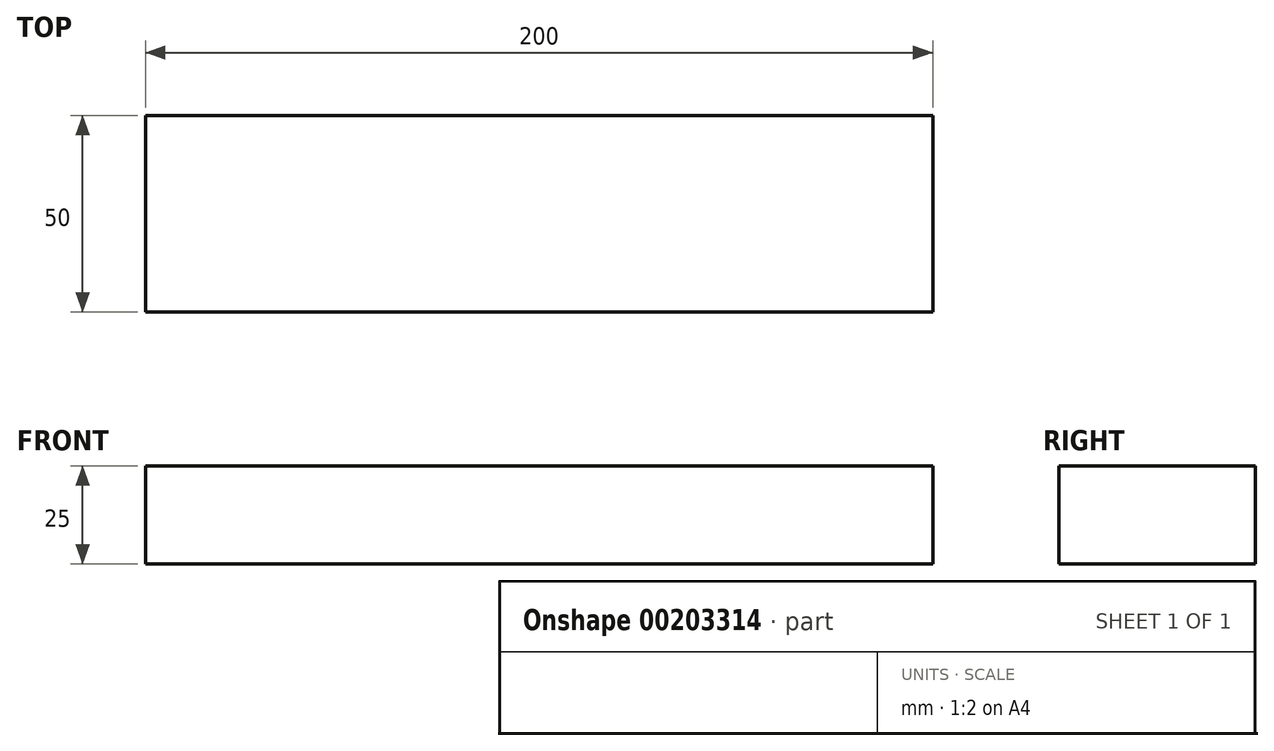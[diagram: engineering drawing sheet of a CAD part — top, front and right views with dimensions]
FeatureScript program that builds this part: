
annotation { "Feature Type Name" : "Feature", "Feature Type Description" : "" }
export const myFeature = defineFeature(function(context is Context, id is Id, definition is map)
    precondition{}
    {
        {
            var Q0;
            Q0=qCreatedBy(makeId("Front.planeOp"),FACE);
            var sketch = newSketch(context, id + "F0", { "sketchPlane" : qUnion([Q0])});
            skLineSegment(sketch, "E0.bottom", {"start": v(100, -12.5) * mm, "end": v(-100, -12.5) * mm});
            skLineSegment(sketch, "E0.top", {"start": v(100, 12.5) * mm, "end": v(-100, 12.5) * mm});
            skLineSegment(sketch, "E0.left", {"start": v(100, -12.5) * mm, "end": v(100, 12.5) * mm});
            skLineSegment(sketch, "E0.right", {"start": v(-100, -12.5) * mm, "end": v(-100, 12.5) * mm});
            skPoint(sketch, "E0.middle", {"position": v(0, 0) * mm});
            skSolve(sketch);
        }
        {
            var Q0;
            Q0=makeQuery(id+"F0.imprint","IMPRINT",FACE,{"disambiguationData":[TD([[makeQuery(id+"F0.imprint","IMPRINT",EDGE,{"derivedFrom":sQuery(id+"F0.wireOp",EDGE,"E0.bottom")}),-1.0]])]});
            extrude(context, id + "F1", {"entities" : qUnion([Q0]), "depth" : 50 * mm});
        }
    });
